# Revit family: BE_55010_de_DE
name_source: partatom
category: Leuchten
revit_build: Autodesk Revit 2015 (Build: 20150704_0715(x64)
units: mm (PartAtom-declared; Revit-internal decimal feet)

## types (1)
- BEGA_55010_Grafit_K3
    AC/DC = AC/DC
    Aktualisierung = 2015-11-11T04:07:44
    BEGA_Dummy = Nein
    BEGA_IES = Ja
    BEGA_Intern = Ja
    BEGA_Intern_Konstruktion = Ja
    BEGA_Intern_an = Ja
    BEGA_Intern_aus = Ja
    Beschreibung = Gartenleuchte
    Beschreibung_Sonderanfertigung = Hier können Sie Informationen zur Sonderanfertigung eintragen.
    Bestellnummer = 55010
    CE_Konformität = ja
    Datei für fotometrisches Netz = BE_55010.IES
    ENEC = ja
    Energieeffizienzklasse = LED A++ - A
    Farbfilter = 16777215
    Farbtemperatur = 3000 K
    Farbtemperaturverschiebung bei Dämpfen der Lampe = <Keine Auswahl>
    Farbwiedergabeindex = Ra > 80
    Frequenz = 0/50-60 Hz
    Gewicht = 1.2 kg
    Hersteller = BEGA
    LED_Modulbezeichnung = LED-0123/830
    Lampe = LED 3.2 W
    Lampenlichtstrom = 245 lm
    Lastklassifizierung = Beleuchtung
    Lebensdauerkriterien = L70 = 50.000 h
    Leuchtenlichtstrom = 171 lm
    Logo = BEGA_Logo.png
    Material_11 = BEGA_Glas_opal
    Modell = 55010
    Neigungswinkel = 0.00°
    Produktdatenblatt = http://www.bega.de
    Scheinlast = 0 VA
    Schutzart = IP 65
    Schutzklasse = I
    Sonderanfertigung = Nein
    Spannung = 0 V
    Typenbild = 55010.png
    URL = http://www.bega.de
    Vorgabe-Ansicht = 0 mm  [stored 0 ft]

note: [stored X ft] marks values corroborated as IEEE doubles in the binary element streams (Revit-internal decimal feet)
